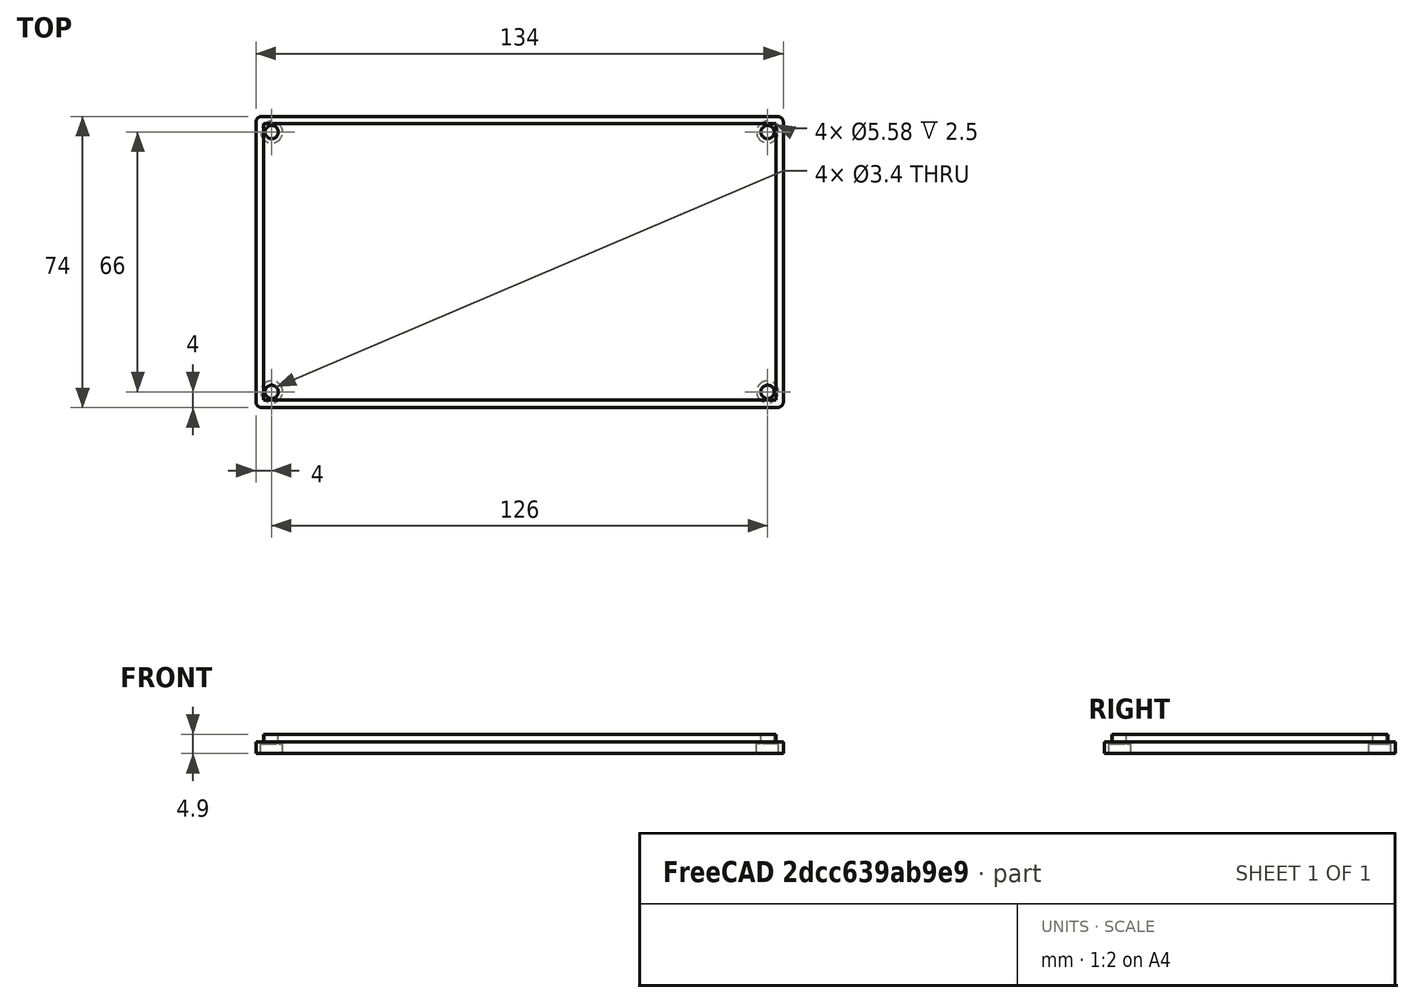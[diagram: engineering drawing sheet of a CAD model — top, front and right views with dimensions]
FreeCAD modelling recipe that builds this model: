
FCSTD DOCUMENT  (FreeCAD 0.19R24291 (Git))
Label: powerbox_top
License: All rights reserved
LicenseURL: http://en.wikipedia.org/wiki/All_rights_reserved
objects: Sketcher::SketchObject×3, PartDesign::Pad×2, PartDesign::Mirrored×2, Spreadsheet::Sheet×1, PartDesign::Plane×1, PartDesign::Hole×1, PartDesign::MultiTransform×1, PartDesign::Fillet×1, PartDesign::Body×1, Mesh::Feature×1
note: 16 computed .brp shape members not serialized (recipe doc carries the construction recipe); baked Part::Feature solids carry a one-line shape summary decoded from their .brp

FEATURE [Sketcher::SketchObject] Sketch
  FullyConstrained = true
  MapMode = 5
  Support = -> [XY_Plane]
  expr: Constraints[8] = <<PowerboxTopDims>>.length / 2 + <<PowerboxTopDims>>.thickness
  expr: Constraints[9] = <<PowerboxTopDims>>.length / 2 + <<PowerboxTopDims>>.thickness
  expr: Constraints[10] = <<PowerboxTopDims>>.width / 2 + <<PowerboxTopDims>>.thickness
  expr: Constraints[11] = <<PowerboxTopDims>>.width / 2 + <<PowerboxTopDims>>.thickness
  sketch-geometry (4):
    g0: LineSegment StartX=-67 StartY=37 StartZ=0 EndX=67 EndY=37 EndZ=0
    g1: LineSegment StartX=67 StartY=37 StartZ=0 EndX=67 EndY=-37 EndZ=0
    g2: LineSegment StartX=67 StartY=-37 StartZ=0 EndX=-67 EndY=-37 EndZ=0
    g3: LineSegment StartX=-67 StartY=-37 StartZ=0 EndX=-67 EndY=37 EndZ=0
  constraints (12):
    c: Coincident(g0,g1)
    c: Coincident(g1,g2)
    c: Coincident(g2,g3)
    c: Coincident(g3,g0)
    c: Horizontal(g0)
    c: Horizontal(g2)
    c: Vertical(g1)
    c: Vertical(g3)
    c: Distance(g-1,g1) = 67
    c: Distance(g-1,g3) = 67
    c: Distance(g-1,g0) = 37
    c: Distance(g-1,g2) = 37
FEATURE [Spreadsheet::Sheet] Spreadsheet  label="PowerboxTopDims"
  cells = A1=Width; B1(width)==70mm; A2=Length; B2(length)==130mm; A3=Height; B3(height)==3mm; A4=Thickness; B4(thickness)==2mm
FEATURE [PartDesign::Pad] Pad
  Direction = (1,1,1)
  Length = 3
  Length2 = 100
  Profile = -> Sketch
  Type = 0
  expr: Length = <<PowerboxTopDims>>.height
FEATURE [PartDesign::Plane] DatumPlane
  Length = 153.916
  MapMode = 5
  Placement = pos=(0,0,3) rot=(0,0,1;0rad)
  ResizeMode = 0
  Support = -> [Pad]
  Width = 93.9158
FEATURE [Sketcher::SketchObject] Sketch001
  FullyConstrained = true
  MapMode = 5
  Placement = pos=(0,0,3) rot=(0,0,1;0rad)
  Support = -> [DatumPlane]
  expr: Constraints[8] = <<PowerboxTopDims>>.length / 2 + 0.1mm
  expr: Constraints[9] = <<PowerboxTopDims>>.length / 2 + 0.1mm
  expr: Constraints[10] = <<PowerboxTopDims>>.width / 2 + 0.1mm
  expr: Constraints[11] = <<PowerboxTopDims>>.width / 2 + 0.1mm
  sketch-geometry (4):
    g0: LineSegment StartX=-65.1 StartY=35.1 StartZ=0 EndX=65.1 EndY=35.1 EndZ=0
    g1: LineSegment StartX=65.1 StartY=35.1 StartZ=0 EndX=65.1 EndY=-35.1 EndZ=0
    g2: LineSegment StartX=65.1 StartY=-35.1 StartZ=0 EndX=-65.1 EndY=-35.1 EndZ=0
    g3: LineSegment StartX=-65.1 StartY=-35.1 StartZ=0 EndX=-65.1 EndY=35.1 EndZ=0
  constraints (12):
    c: Coincident(g0,g1)
    c: Coincident(g1,g2)
    c: Coincident(g2,g3)
    c: Coincident(g3,g0)
    c: Horizontal(g0)
    c: Horizontal(g2)
    c: Vertical(g1)
    c: Vertical(g3)
    c: Distance(g-1,g1) = 65.1
    c: Distance(g-1,g3) = 65.1
    c: Distance(g-1,g0) = 35.1
    c: Distance(g-1,g2) = 35.1
FEATURE [PartDesign::Pad] Pad001
  BaseFeature = -> Pad
  Direction = (1,1,1)
  Length = 1.9
  Length2 = 100
  Profile = -> Sketch001
  Type = 0
FEATURE [Sketcher::SketchObject] Sketch002
  FullyConstrained = false
  MapMode = 5
  Support = -> [XY_Plane]
  expr: Constraints[0] = <<PowerboxTopDims>>.length / 2 - <<PowerboxTopDims>>.thickness
  expr: Constraints[1] = <<PowerboxTopDims>>.width / 2 - <<PowerboxTopDims>>.thickness
  sketch-geometry (1):
    g0: Circle CenterX=-63 CenterY=33 CenterZ=0 NormalX=0 NormalY=0 NormalZ=1 AngleXU=0 Radius=2.81165
  constraints (2):
    c: DistanceX(g0,g-1) = 63
    c: DistanceY(g-1,g0) = 33
FEATURE [PartDesign::Hole] Hole
  BaseFeature = -> Pad001
  Depth = 25
  DepthType = 0
  Diameter = 3.4
  DrillForDepth = false
  DrillPoint = 1
  DrillPointAngle = 118
  HoleCutCountersinkAngle = 90
  HoleCutCustomValues = false
  HoleCutDepth = 2.5
  HoleCutDiameter = 5.58
  HoleCutType = 1
  ModelActualThread = false
  Profile = -> Sketch002
  Reversed = true
  Tapered = false
  TaperedAngle = 90
  ThreadAngle = 0
  ThreadClass = 0
  ThreadCutOffInner = 0
  ThreadCutOffOuter = 0
  ThreadDirection = 0
  ThreadFit = 0
  ThreadPitch = 0
  ThreadSize = 0
  ThreadType = 0
  Threaded = false
FEATURE [PartDesign::Mirrored] Mirrored
  MirrorPlane = -> Sketch002 [V_Axis]
FEATURE [PartDesign::Mirrored] Mirrored001
  MirrorPlane = -> Sketch002 [H_Axis]
FEATURE [PartDesign::MultiTransform] MultiTransform
  BaseFeature = -> Hole
  Originals = -> [Hole]
  Transformations = -> [Mirrored,Mirrored001]
FEATURE [PartDesign::Fillet] Fillet
  Base = -> MultiTransform [Edge5,Edge1,Edge2,Edge8]
  BaseFeature = -> MultiTransform
  Radius = 1.5
  SupportTransform = false
FEATURE [PartDesign::Body] Body
  Group = -> [Sketch,Pad,DatumPlane,Sketch001,Pad001,Sketch002,Hole,MultiTransform,Mirrored,Mirrored001,Fillet]
  Origin = -> Origin
  Tip = -> Fillet
FEATURE [Mesh::Feature] Mesh  label="Body (Meshed)"
